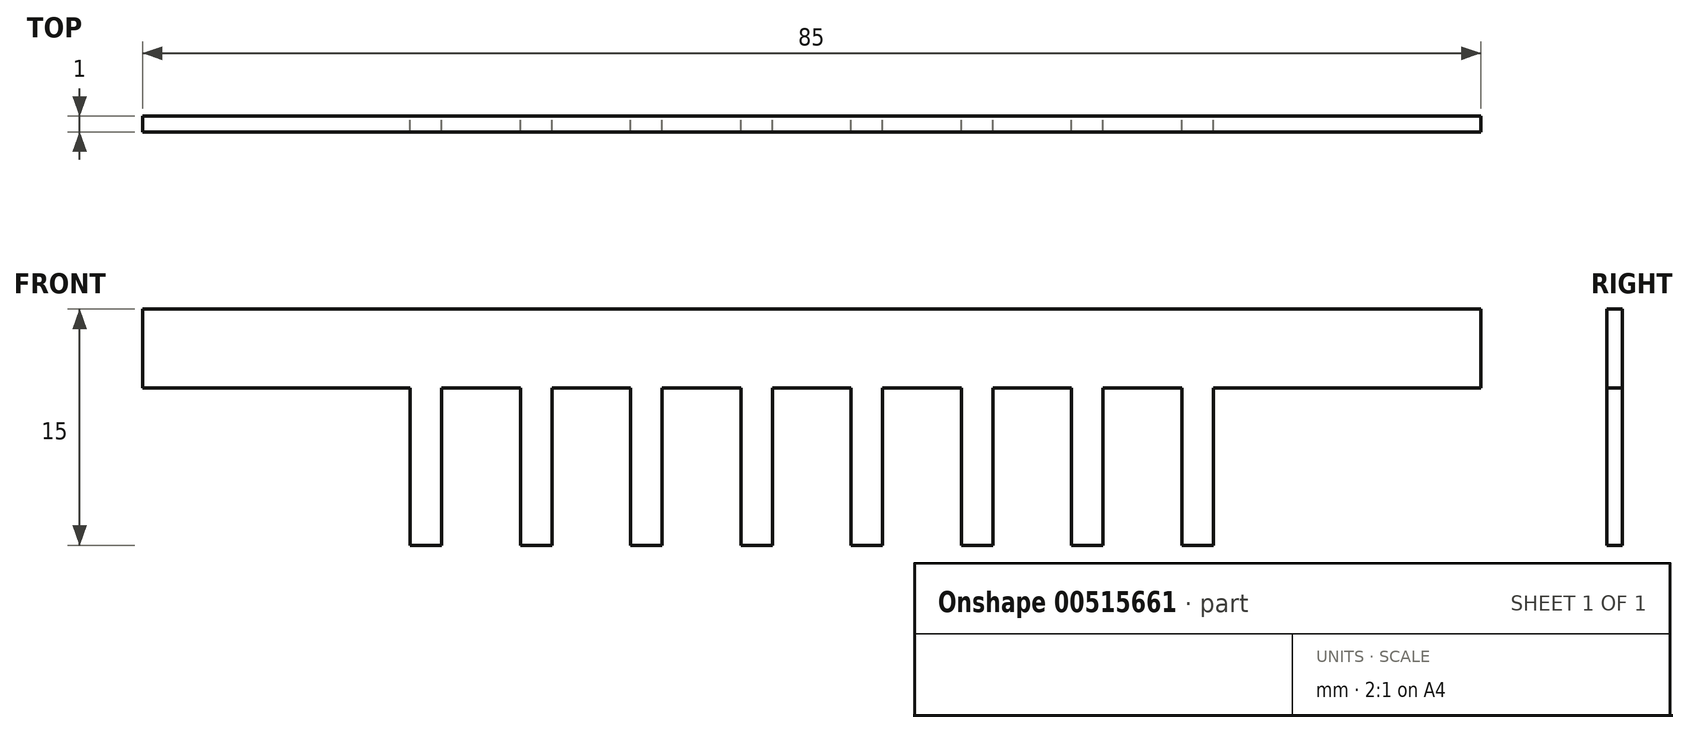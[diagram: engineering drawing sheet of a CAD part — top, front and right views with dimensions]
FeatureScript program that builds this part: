
annotation { "Feature Type Name" : "Feature", "Feature Type Description" : "" }
export const myFeature = defineFeature(function(context is Context, id is Id, definition is map)
    precondition{}
    {
        {
            var Q0;
            Q0=qCreatedBy(makeId("Front.planeOp"),FACE);
            var sketch = newSketch(context, id + "F0", { "sketchPlane" : qUnion([Q0])});
            skLineSegment(sketch, "E0.top", {"start": v(42.5, 5) * mm, "end": v(-42.5, 5) * mm});
            skLineSegment(sketch, "E0.left", {"start": v(42.5, 0) * mm, "end": v(42.5, 5) * mm});
            skLineSegment(sketch, "E0.right", {"start": v(-42.5, 0) * mm, "end": v(-42.5, 5) * mm});
            skPoint(sketch, "E0.middle", {"position": v(0, 0) * mm});
            skLineSegment(sketch, "E1", {"start": v(-2.5, 0) * mm, "end": v(-2.5, -10) * mm});
            skLineSegment(sketch, "E2", {"start": v(-4.5, 0) * mm, "end": v(-4.5, -10) * mm});
            skLineSegment(sketch, "E3", {"start": v(-9.5, 0) * mm, "end": v(-9.5, -10) * mm});
            skLineSegment(sketch, "E4", {"start": v(-11.5, 0) * mm, "end": v(-11.5, -10) * mm});
            skLineSegment(sketch, "E5", {"start": v(-16.5, 0) * mm, "end": v(-16.5, -10) * mm});
            skLineSegment(sketch, "E6", {"start": v(-18.5, 0) * mm, "end": v(-18.5, -10) * mm});
            skLineSegment(sketch, "E7", {"start": v(-23.5, 0) * mm, "end": v(-23.5, -10) * mm});
            skLineSegment(sketch, "E8", {"start": v(-25.5, 0) * mm, "end": v(-25.5, -10) * mm});
            skLineSegment(sketch, "E9", {"start": v(-23.5, 0) * mm, "end": v(-18.5, 0) * mm});
            skLineSegment(sketch, "E10", {"start": v(-16.5, 0) * mm, "end": v(-11.5, 0) * mm});
            skLineSegment(sketch, "E11", {"start": v(-9.5, 0) * mm, "end": v(-4.5, 0) * mm});
            skLineSegment(sketch, "E12.MirrorCS", {"start": v(2.5, 0) * mm, "end": v(2.5, -10) * mm});
            skLineSegment(sketch, "E13.MirrorCS", {"start": v(4.5, 0) * mm, "end": v(4.5, -10) * mm});
            skLineSegment(sketch, "E14.MirrorCS", {"start": v(9.5, 0) * mm, "end": v(9.5, -10) * mm});
            skLineSegment(sketch, "E15.MirrorCS", {"start": v(11.5, 0) * mm, "end": v(11.5, -10) * mm});
            skLineSegment(sketch, "E16.MirrorCS", {"start": v(16.5, 0) * mm, "end": v(16.5, -10) * mm});
            skLineSegment(sketch, "E17.MirrorCS", {"start": v(18.5, 0) * mm, "end": v(18.5, -10) * mm});
            skLineSegment(sketch, "E18.MirrorCS", {"start": v(23.5, 0) * mm, "end": v(23.5, -10) * mm});
            skLineSegment(sketch, "E19.MirrorCS", {"start": v(25.5, 0) * mm, "end": v(25.5, -10) * mm});
            skLineSegment(sketch, "E20.MirrorCS", {"start": v(23.5, 0) * mm, "end": v(18.5, 0) * mm});
            skLineSegment(sketch, "E21.MirrorCS", {"start": v(16.5, 0) * mm, "end": v(11.5, 0) * mm});
            skLineSegment(sketch, "E22.MirrorCS", {"start": v(9.5, 0) * mm, "end": v(4.5, 0) * mm});
            skLineSegment(sketch, "E23", {"start": v(-2.5, 0) * mm, "end": v(2.5, 0) * mm});
            skLineSegment(sketch, "E24.trimOffspring", {"start": v(-23.5, -10) * mm, "end": v(-25.5, -10) * mm});
            skLineSegment(sketch, "E25.trimOffspring", {"start": v(-16.5, -10) * mm, "end": v(-18.5, -10) * mm});
            skLineSegment(sketch, "E26.trimOffspring", {"start": v(-9.5, -10) * mm, "end": v(-11.5, -10) * mm});
            skLineSegment(sketch, "E27.trimOffspring", {"start": v(-2.5, -10) * mm, "end": v(-4.5, -10) * mm});
            skLineSegment(sketch, "E28.trimOffspring", {"start": v(4.5, -10) * mm, "end": v(2.5, -10) * mm});
            skLineSegment(sketch, "E29.trimOffspring", {"start": v(11.5, -10) * mm, "end": v(9.5, -10) * mm});
            skLineSegment(sketch, "E30.trimOffspring", {"start": v(18.5, -10) * mm, "end": v(16.5, -10) * mm});
            skLineSegment(sketch, "E31", {"start": v(-42.5, 0) * mm, "end": v(-25.5, 0) * mm});
            skLineSegment(sketch, "E32.MirrorCS", {"start": v(42.5, 0) * mm, "end": v(25.5, 0) * mm});
            skLineSegment(sketch, "E33.trimOffspring", {"start": v(25.5, -10) * mm, "end": v(23.5, -10) * mm});
            skSolve(sketch);
        }
        {
            var Q0;
            Q0 = qSketchRegion(id + "F0", true);
            extrude(context, id + "F1", {"entities" : qUnion([Q0]), "depth" : 1 * mm, "offsetDistance" : 25 * mm});
        }
    });
